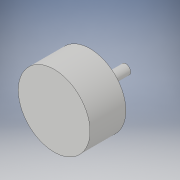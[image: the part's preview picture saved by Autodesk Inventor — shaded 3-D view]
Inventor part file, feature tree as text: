
AUTODESK INVENTOR PART (.ipt)
format: ipt  version: 2019 (Build 230136000, 136)  size: 98,304 bytes
history: native  units: mm
features: extrude x2, sketch x2
ambient origin geometry x8: Origin, YZ Plane, XZ Plane, XY Plane, X Axis, Y Axis, Z Axis, Center Point
bodies: Solid1 (feature_tree)
feature tree (4):
  extrude  "Extrusion1"  Depth=60.0mm
  extrude  "Extrusion2"  [1 undecoded]
  sketch  "Sketch1"  dims[d0=30.0mm d1=0.0mm d2=60.0mm]
  sketch  "Sketch2"  dims[d3=30.0mm d4=0.0mm]
note: 1 required parameter value undecoded (feature->parameter linkage not recoverable at this tier; creation-order binding heuristic only, values carry confidence <= 0.55)
